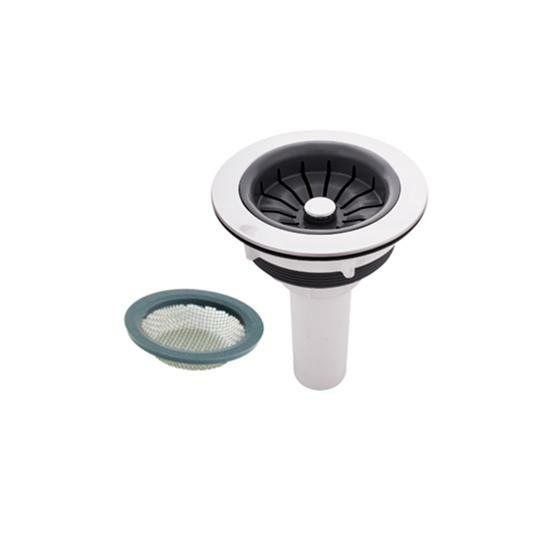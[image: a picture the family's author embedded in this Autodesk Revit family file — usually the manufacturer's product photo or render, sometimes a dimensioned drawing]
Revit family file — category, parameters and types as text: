
# Revit family: 01-31707-11 LAVAPLATOS EN ACERO POCETA 50 X 34 CM
name_source: partatom
category: Aparatos sanitarios
revit_build: Autodesk Revit 2018 (Build: 20170223_1515(x64)
units: mm (PartAtom-declared; Revit-internal decimal feet)

## family parameters
Anfitrión = Cara
Compartido = No
Corte con vacíos al cargar = No
Cota de conector redondo = Diámetro de uso
Número OmniClass = 23.31.11.00
Punto de cálculo de habitación = No
Tipo de pieza = Normal

## types (1)
- 01-31707-11
    Acero inox = Acero inoxidable
    Alto = 170 mm  [stored 0.557743 ft]
    Ancho = 500 mm  [stored 1.64042 ft]
    Conexión AC = Sí
    Conexión AF = Sí
    Conexión de residuos = No
    Conexión de ventilación = No
    Descripción = Lavaplatos en acero
    Elevación por defecto = 0 mm  [stored 0 ft]
    Fabricante = Gricol
    Imagen de tipo = <Ninguno>
    Largo = 340 mm  [stored 1.11549 ft]
    Link Ficha Tecnica = No existe
    Modelo = 01-31707-11
    Product Name = LAVAPLATOS EN ACERO POCETA 50 X 34 CM
    URL = https://www.gricol.com

note: [stored X ft] marks values corroborated as IEEE doubles in the binary element streams (Revit-internal decimal feet)

## geometry (parser evidence)
native form markers: Blend x2, Sweep x14
no freeform markers — native parametric forms only
